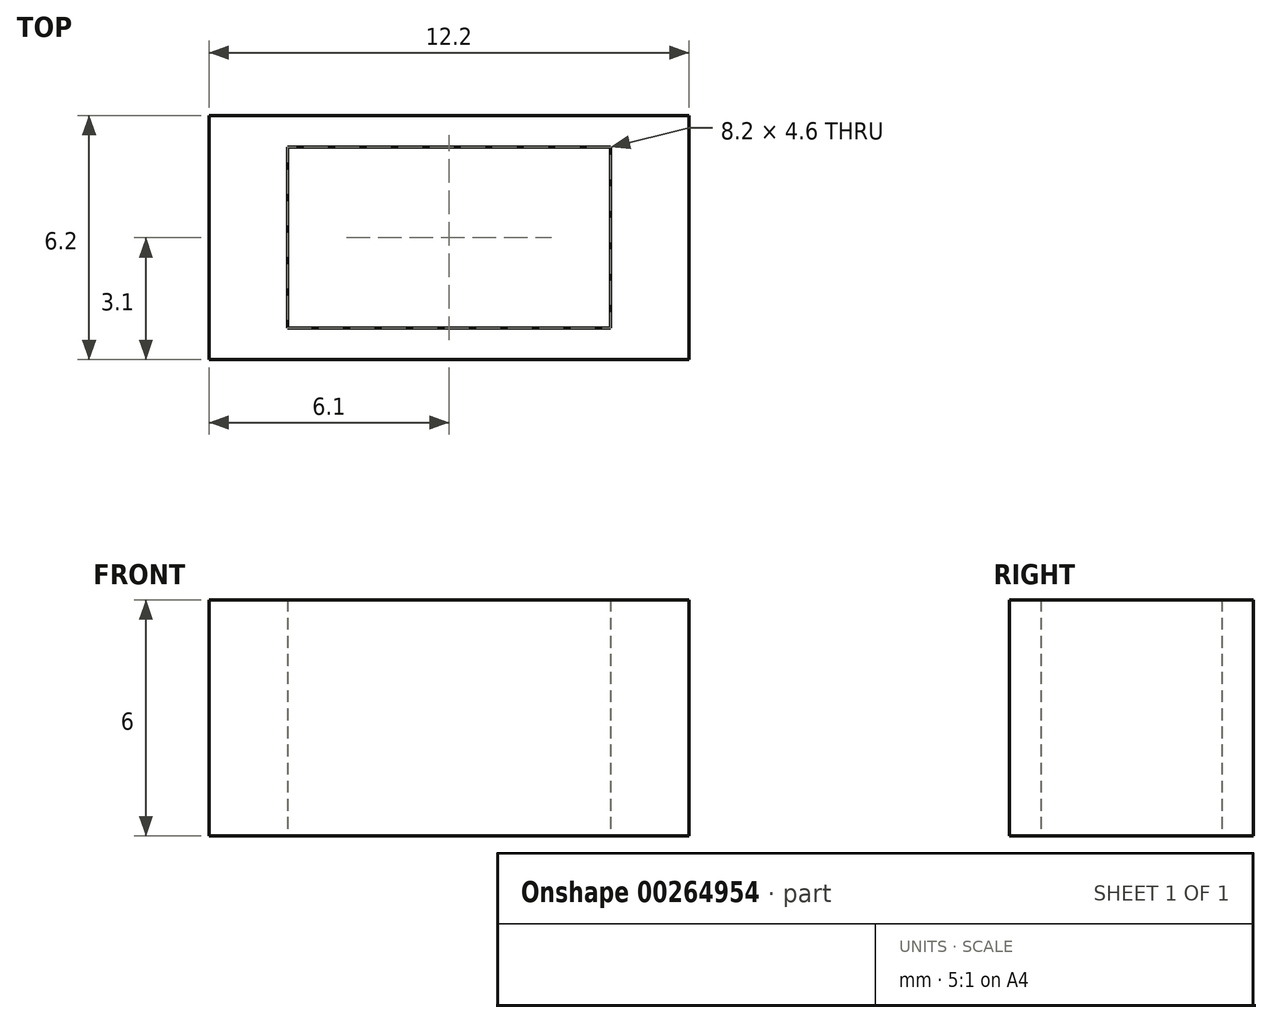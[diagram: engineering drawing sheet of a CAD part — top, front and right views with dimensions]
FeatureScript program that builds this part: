
annotation { "Feature Type Name" : "Feature", "Feature Type Description" : "" }
export const myFeature = defineFeature(function(context is Context, id is Id, definition is map)
    precondition{}
    {
        {
            var Q0;
            Q0=qCreatedBy(makeId("Top.planeOp"),FACE);
            var sketch = newSketch(context, id + "F0", { "sketchPlane" : qUnion([Q0])});
            skLineSegment(sketch, "E0.bottom", {"start": v(-6.1, 3.1) * mm, "end": v(6.1, 3.1) * mm});
            skLineSegment(sketch, "E0.top", {"start": v(-6.1, -3.1) * mm, "end": v(6.1, -3.1) * mm});
            skLineSegment(sketch, "E0.left", {"start": v(-6.1, 3.1) * mm, "end": v(-6.1, -3.1) * mm});
            skLineSegment(sketch, "E0.right", {"start": v(6.1, 3.1) * mm, "end": v(6.1, -3.1) * mm});
            skLineSegment(sketch, "E1.bottom", {"start": v(-4.1, 2.3) * mm, "end": v(4.1, 2.3) * mm});
            skLineSegment(sketch, "E1.top", {"start": v(-4.1, -2.3) * mm, "end": v(4.1, -2.3) * mm});
            skLineSegment(sketch, "E1.left", {"start": v(-4.1, 2.3) * mm, "end": v(-4.1, -2.3) * mm});
            skLineSegment(sketch, "E1.right", {"start": v(4.1, 2.3) * mm, "end": v(4.1, -2.3) * mm});
            skLineSegment(sketch, "E2", {"start": v(0, -11.06) * mm, "end": v(0, 10.6) * mm, "construction": true});
            skLineSegment(sketch, "E3", {"start": v(-18.52, 0) * mm, "end": v(20.91, 0) * mm, "construction": true});
            skSolve(sketch);
        }
        {
            var Q0;
            Q0 = qSketchRegion(id + "F0", true);
            extrude(context, id + "F1", {"entities" : qUnion([Q0]), "depth" : 6 * mm});
        }
    });
